# Revit family: FU_Inspec_Aperi_6-1
name_source: partatom
category: Furniture
units: mm (PartAtom-declared; Revit-internal decimal feet)

## family parameters
Always vertical = Yes
Cut with Voids When Loaded = No
OmniClass Number = 23.40.20.00
OmniClass Title = General Furniture and Specialties
Room Calculation Point = No
Shared = No
Work Plane-Based = No

## types (1)
- aperi 6.1
    Assembly Code = E2020
    Default Elevation = 0 mm  [stored 0 ft]
    Depth = 800 mm  [stored 2.62467 ft]
    Description = Easy chair with upholstered polyurethane foam padding on a powder coated black metal base with adjustable feet.
    Height = 780 mm  [stored 2.55906 ft]
    Keynote = 46.B
    Legs Material = Metal - Black - Matte
    Length = 760 mm
    Manufacturer = Inspec
    Model = aperi 6.1
    Seat Material = Fabric - Dark Purple Woven
    URL = https://inspecfurniture.com
    Weight = 32 Kg
    Width = 800 mm  [stored 2.62467 ft]

note: [stored X ft] marks values corroborated as IEEE doubles in the binary element streams (Revit-internal decimal feet)

## geometry (parser evidence)
native form markers: Sweep x2
no freeform markers — native parametric forms only
